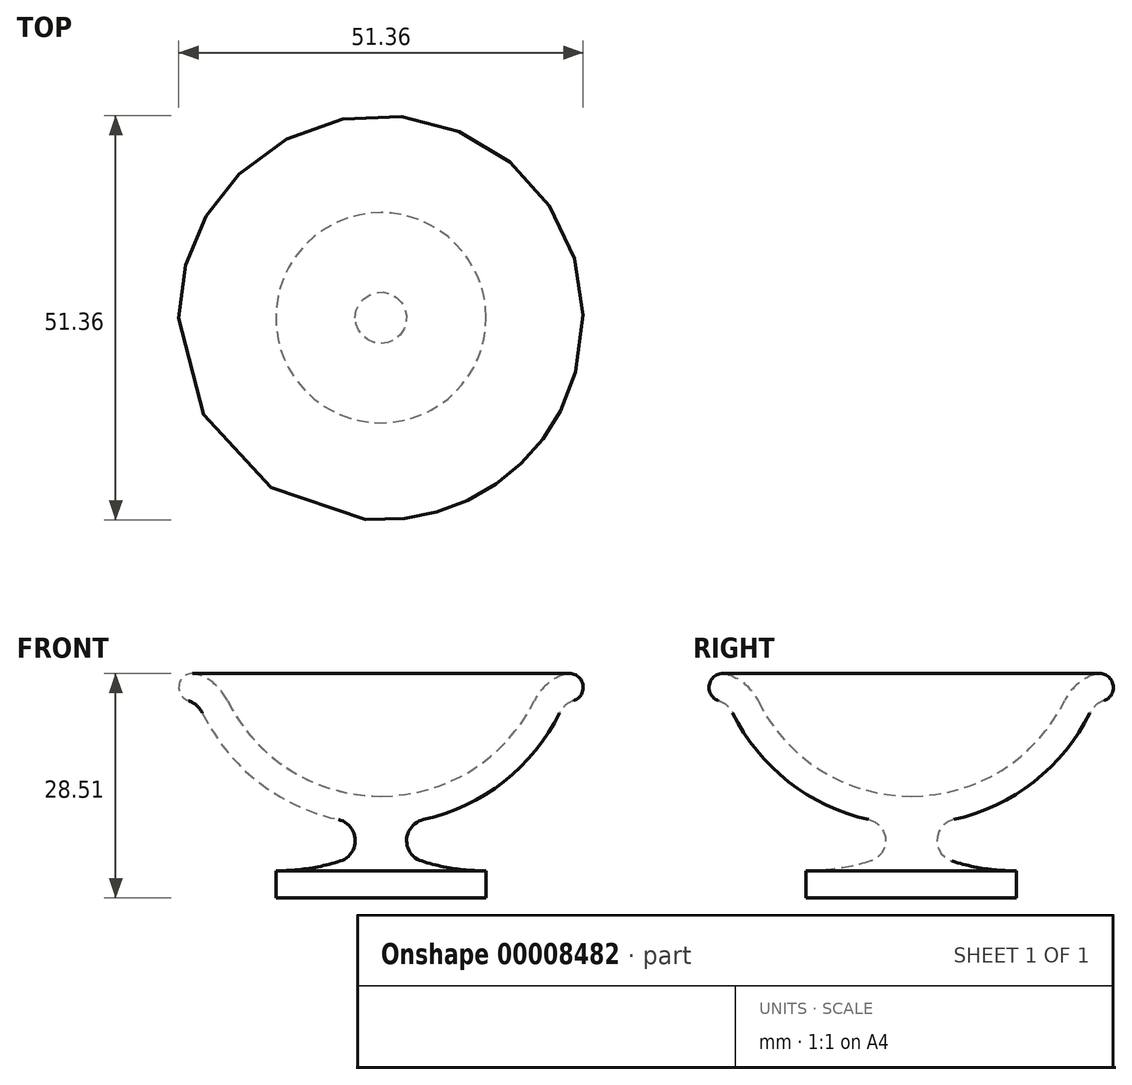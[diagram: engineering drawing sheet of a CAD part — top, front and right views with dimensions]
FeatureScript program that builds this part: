
annotation { "Feature Type Name" : "Feature", "Feature Type Description" : "" }
export const myFeature = defineFeature(function(context is Context, id is Id, definition is map)
    precondition{}
    {
        {
            var Q0;
            Q0=qCreatedBy(makeId("Front.planeOp"),FACE);
            var sketch = newSketch(context, id + "F0", { "sketchPlane" : qUnion([Q0])});
            skLineSegment(sketch, "E0", {"start": v(0, 0) * mm, "end": v(-13.35, 0) * mm});
            skLineSegment(sketch, "E1", {"start": v(-13.35, 0) * mm, "end": v(-13.35, 3.42) * mm});
            skLineSegment(sketch, "E2", {"start": v(0, 0) * mm, "end": v(0, 12.92) * mm});
            skArc(sketch, "E3", {"start": v(-13.35, 3.42) * mm, "mid": v(-9.22, 3.74) * mm, "end": v(-5.19, 4.67) * mm});
            skArc(sketch, "E4", {"start": v(-5.19, 4.67) * mm, "mid": v(-3.27, 7.4) * mm, "end": v(-5.41, 9.95) * mm});
            skArc(sketch, "E5", {"start": v(-5.41, 9.95) * mm, "mid": v(-15.6, 14.75) * mm, "end": v(-22.7, 23.5) * mm});
            skArc(sketch, "E6", {"start": v(-22.7, 23.5) * mm, "mid": v(-23.42, 24.45) * mm, "end": v(-24.47, 25.05) * mm});
            skArc(sketch, "E7", {"start": v(-24.47, 25.05) * mm, "mid": v(-25.6, 27.3) * mm, "end": v(-23.35, 28.42) * mm});
            skArc(sketch, "E8", {"start": v(-23.35, 28.42) * mm, "mid": v(-21.09, 27.13) * mm, "end": v(-19.5, 25.07) * mm});
            skArc(sketch, "E9", {"start": v(-19.5, 25.07) * mm, "mid": v(-11.49, 16.2) * mm, "end": v(0, 12.92) * mm});
            skLineSegment(sketch, "E10", {"start": v(0, 12.92) * mm, "end": v(-10.41, 12.92) * mm, "construction": true});
            skLineSegment(sketch, "E11", {"start": v(-13.35, 3.42) * mm, "end": v(-3.91, 3.42) * mm});
            skSolve(sketch);
        }
        {
            var Q0;
            Q0=makeQuery(id+"F0.imprint","IMPRINT",FACE,{"disambiguationData":[TD([[makeQuery(id+"F0.imprint","IMPRINT",EDGE,{"derivedFrom":sQuery(id+"F0.wireOp",EDGE,"E0")}),-1.0]])]});
            var Q1;
            Q1=sQuery(id+"F0.wireOp",EDGE,"E2");
            revolve(context, id + "F1", {"entities" : qUnion([Q0]), "axis" : qUnion([Q1]), "revolveType" : RevolveType.FULL});
        }
    });
